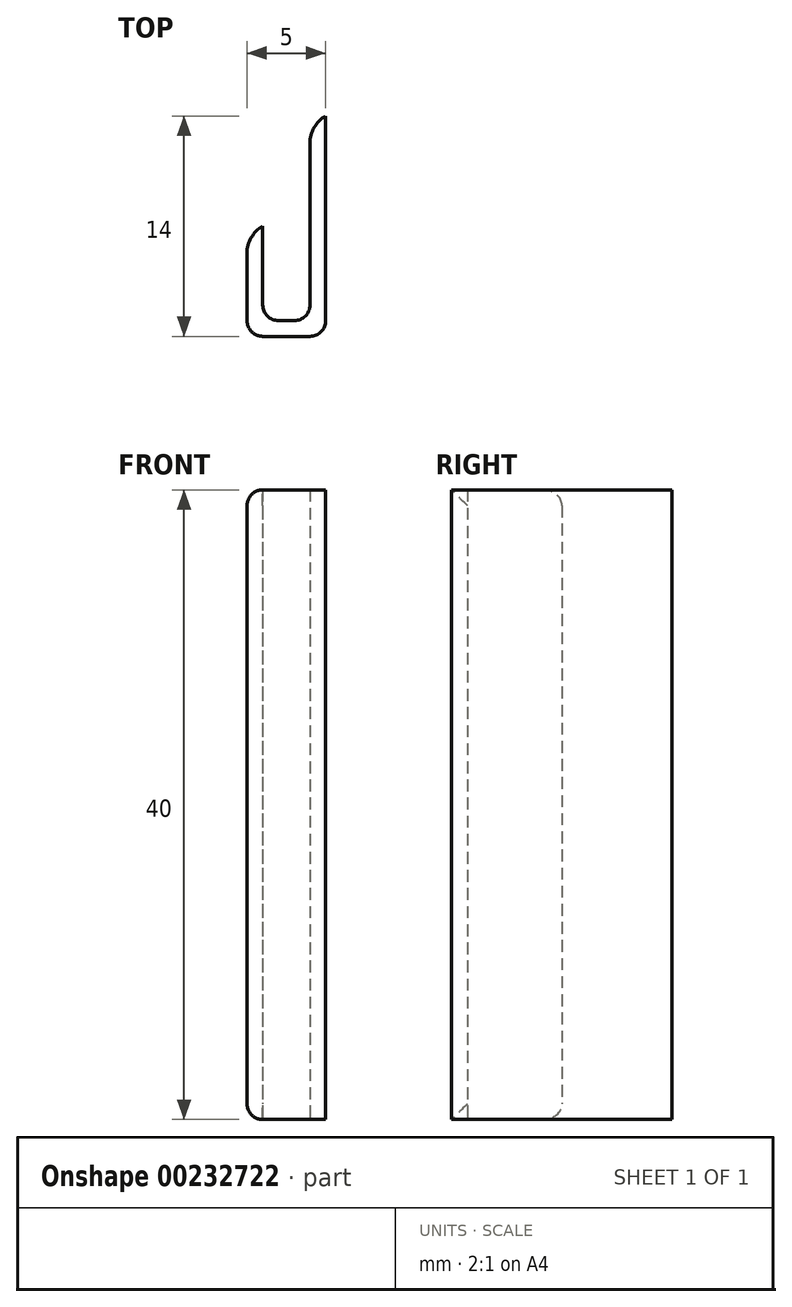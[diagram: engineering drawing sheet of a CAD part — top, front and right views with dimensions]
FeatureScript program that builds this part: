
annotation { "Feature Type Name" : "Feature", "Feature Type Description" : "" }
export const myFeature = defineFeature(function(context is Context, id is Id, definition is map)
    precondition{}
    {
        {
            var Q0;
            Q0=qCreatedBy(makeId("Top.planeOp"),FACE);
            var sketch = newSketch(context, id + "F0", { "sketchPlane" : qUnion([Q0])});
            skLineSegment(sketch, "E0", {"start": v(0, 0) * mm, "end": v(0, 14) * mm});
            skLineSegment(sketch, "E1", {"start": v(0, 0) * mm, "end": v(-5, 0) * mm});
            skLineSegment(sketch, "E2", {"start": v(-5, 0) * mm, "end": v(-5, 7) * mm});
            skLineSegment(sketch, "E3", {"start": v(-5, 7) * mm, "end": v(-4, 7) * mm});
            skLineSegment(sketch, "E4", {"start": v(-4, 7) * mm, "end": v(-4, 1) * mm});
            skLineSegment(sketch, "E5", {"start": v(-4, 1) * mm, "end": v(-1, 1) * mm});
            skLineSegment(sketch, "E6", {"start": v(-1, 1) * mm, "end": v(-1, 14) * mm});
            skLineSegment(sketch, "E7", {"start": v(-1, 14) * mm, "end": v(0, 14) * mm});
            skSolve(sketch);
        }
        {
            var Q0;
            Q0=qSketchRegion(id+"F0",true);
            extrude(context, id + "F1", {"entities" : qUnion([Q0]), "depth" : 40 * mm, "offsetDistance" : 25 * mm});
        }
        {
            var Q0;
            Q0=makeQuery(id+"F1.opExtrude","SWEPT_EDGE",EDGE,{"disambiguationData":[OSD([sQuery(id+"F0.wireOp",EDGE,"E2"),sQuery(id+"F0.wireOp",EDGE,"E3")])]});
            var Q1;
            Q1=makeQuery(id+"F1.opExtrude","SWEPT_EDGE",EDGE,{"disambiguationData":[OSD([sQuery(id+"F0.wireOp",EDGE,"E6"),sQuery(id+"F0.wireOp",EDGE,"E7")])]});
            fillet(context, id + "F2", {"entities" : qUnion([Q0, Q1]), "radius" : 2 * mm, "tangentPropagation" : true, "allowEdgeOverflow" : false});
        }
        {
            var Q0;
            Q0=makeQuery(id+"F1.opExtrude","CAP_EDGE",EDGE,{"disambiguationData":[OSD([sQuery(id+"F0.wireOp",EDGE,"E2")])],"isStart":false});
            var Q1;
            Q1=makeQuery(id+"F1.opExtrude","CAP_EDGE",EDGE,{"disambiguationData":[OSD([sQuery(id+"F0.wireOp",EDGE,"E2")])],"isStart":true});
            var Q2;
            Q2=makeQuery(id+"F1.opExtrude","SWEPT_EDGE",EDGE,{"disambiguationData":[OSD([sQuery(id+"F0.wireOp",EDGE,"E1"),sQuery(id+"F0.wireOp",EDGE,"E2")])]});
            var Q3;
            Q3=makeQuery(id+"F1.opExtrude","SWEPT_EDGE",EDGE,{"disambiguationData":[OSD([sQuery(id+"F0.wireOp",EDGE,"E0"),sQuery(id+"F0.wireOp",EDGE,"E1")])]});
            var Q4;
            Q4=makeQuery(id+"F1.opExtrude","SWEPT_EDGE",EDGE,{"disambiguationData":[OSD([sQuery(id+"F0.wireOp",EDGE,"E4"),sQuery(id+"F0.wireOp",EDGE,"E5")])]});
            var Q5;
            Q5=makeQuery(id+"F1.opExtrude","SWEPT_EDGE",EDGE,{"disambiguationData":[OSD([sQuery(id+"F0.wireOp",EDGE,"E5"),sQuery(id+"F0.wireOp",EDGE,"E6")])]});
            fillet(context, id + "F3", {"entities" : qUnion([Q0, Q1, Q2, Q3, Q4, Q5]), "radius" : 1 * mm, "tangentPropagation" : true, "allowEdgeOverflow" : false});
        }
    });
